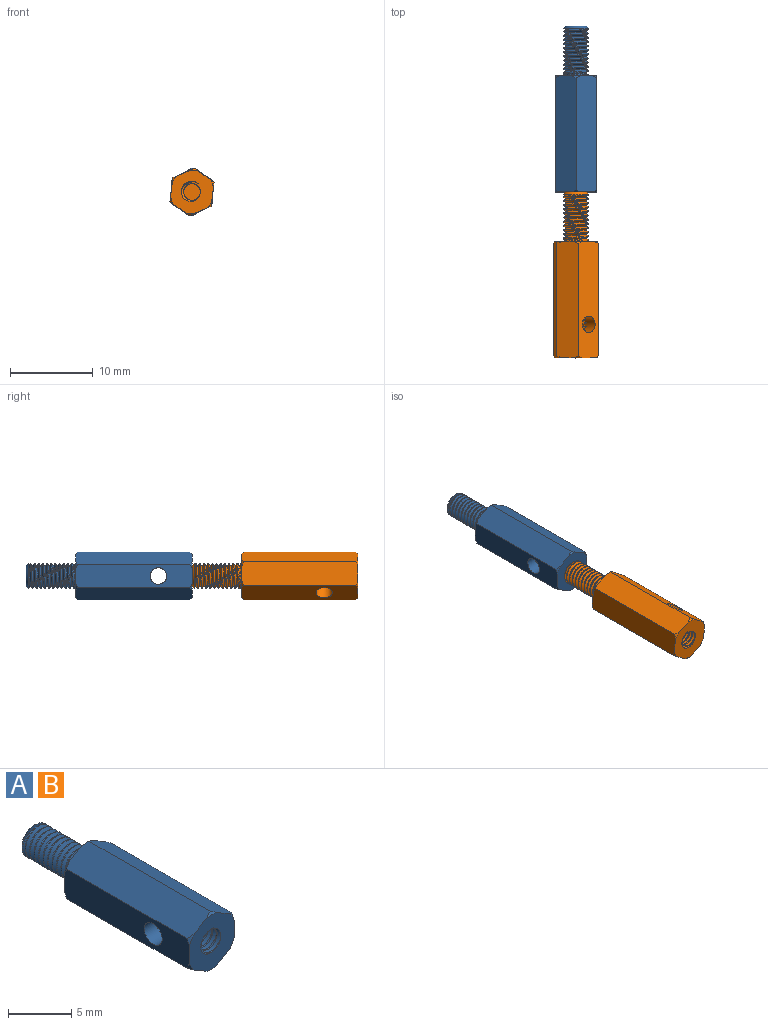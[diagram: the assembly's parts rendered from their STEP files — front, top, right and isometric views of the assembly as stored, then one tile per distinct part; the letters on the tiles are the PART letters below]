
ASSEMBLY  parts=2 mates=1
PART A: 76 faces, bbox 5.6x20.3x5.9 mm
  f0: bspline ~3.57x2.93mm, area 14.5mm2, adj f14,f26,f41,f59,f74,f75
  f1: bspline ~2.57x1.91mm, area 0.6mm2, adj f15,f24,f74,f75
  f2: bspline ~2.2x0.77mm, area 0.4mm2, adj f16,f27,f74,f75
  f3: bspline ~2.2x0.77mm, area 0.3mm2, adj f17,f25,f74,f75
  f4: bspline ~2.2x0.77mm, area 0.4mm2, adj f18,f23,f74,f75
  f5: bspline ~2.2x0.77mm, area 0.4mm2, adj f19,f22,f74,f75
  f6: bspline ~2.2x0.77mm, area 0.6mm2, adj f20,f28,f74,f75
  f7: bspline ~3.57x2.93mm, area 14.6mm2, adj f14,f15,f41,f59,f74,f75
  f8: bspline ~2.2x0.77mm, area 0.6mm2, adj f16,f26,f74,f75
  f9: bspline ~2.2x0.77mm, area 0.4mm2, adj f17,f24,f74,f75
  f10: bspline ~2.2x0.77mm, area 0.3mm2, adj f18,f27,f74,f75
  f11: bspline ~2.2x0.77mm, area 0.3mm2, adj f19,f29,f74,f75
  f12: bspline ~2.2x0.77mm, area 0.4mm2, adj f20,f23,f74,f75
  f13: bspline ~2.57x1.91mm, area 0.6mm2, adj f21,f22,f74,f75
  f14: bspline ~3.4x2.99mm, area 3.7mm2, adj f0,f7,f41,f74
  f15: bspline ~2.61x1.94mm, area 0.2mm2, adj f1,f7,f74,f75
  f16: bspline ~2.24x0.66mm, area 0.2mm2, adj f2,f8,f74,f75
  f17: bspline ~2.24x0.66mm, area 0.1mm2, adj f3,f9,f74,f75
  f18: bspline ~2.24x0.66mm, area 0.1mm2, adj f4,f10,f74,f75
  f19: bspline ~2.24x0.66mm, area 0.1mm2, adj f5,f11,f74,f75
  f20: bspline ~2.24x0.66mm, area 0.2mm2, adj f6,f12,f74,f75
  f21: bspline ~2.61x1.94mm, area 0.2mm2, adj f13,f53,f74,f75
  f22: cylinder r=1mm len=1.16mm, axis (0,-1,0), area 0.1mm2, adj f5,f13,f74,f75
  f23: cylinder r=1mm len=0.65mm, axis (0,-1,0), area 0.1mm2, adj f4,f12,f74,f75
  f24: cylinder r=1mm len=1.11mm, axis (0,-1,0), area 0.1mm2, adj f1,f9,f74,f75
  f25: cylinder r=1mm len=0.1mm, axis (0,-1,0), area 0mm2, adj f3,f74,f75
  f26: cylinder r=1mm len=1.62mm, axis (0,-1,0), area 0.2mm2, adj f0,f8,f74,f75
  f27: cylinder r=1mm len=0.61mm, axis (0,-1,0), area 0.1mm2, adj f2,f10,f74,f75
  f28: cylinder r=1mm len=1.67mm, axis (0,-1,0), area 0.2mm2, adj f6,f54,f74,f75
  f29: cylinder r=1mm len=0.15mm, axis (0,-1,0), area 0mm2, adj f11,f74,f75
  f30: cylinder r=1mm len=0.97mm, axis (0,-1,0), area 0.1mm2, adj f31,f53,f54,f74
  f31: cylinder r=1mm len=2mm, axis (0,-1,0), area 0.8mm2, adj f30,f32,f53,f54
  f32: cylinder r=1mm len=2mm, axis (0,-1,0), area 1.2mm2, adj f31,f33,f53,f55
  f33: cylinder r=1mm len=4mm, axis (0,-1,0), area 24mm2, adj f32,f55,f56,f60,f61
  f34: plane 14.05x2.55mm, normal (0.5,0,0.87), area 40.1mm2, adj f35,f39,f41,f42,f62,f65,f72,f73
  f35: plane 14.05x2.55mm, normal (-0.5,0,0.87), area 40.1mm2, adj f34,f36,f41,f42,f70,f71,f72,f73
  f36: plane 14.05x2.94mm, normal (-1,0,0), area 37mm2, adj f35,f37,f41,f42,f68,f69,f70,f71
  f37: plane 14.05x2.55mm, normal (-0.5,0,-0.87), area 40.1mm2, adj f36,f38,f41,f42,f66,f67,f68,f69
  f38: plane 14.05x2.55mm, normal (0.5,0,-0.87), area 40.1mm2, adj f37,f39,f41,f42,f63,f64,f66,f67
  f39: plane 14.05x2.94mm, normal (1,0,0), area 37mm2, adj f34,f38,f41,f42,f62,f63,f64,f65
  f40: cylinder r=1.5mm len=5.75mm, axis (0,-1,0), area 5mm2, adj f42,f44,f45,f47,f49,f50,f51
  f41: plane 5.41x5.14mm, normal (0,-1,0), area 16.9mm2, adj f0,f7,f14,f34,f35,f36,f37,f38
  f42: plane 5.29x5.01mm, normal (0,1,0), area 14mm2, adj f34,f35,f36,f37,f38,f39,f40,f45
  f43: plane 2.5x2.5mm, normal (0,1,0), area 4.9mm2, adj f44
  f44: cone r=1.5mm half-angle=45deg, axis (0,-1,0), area 3.1mm2, adj f40,f43,f52
  f45: plane 0.04x0.04mm, normal (-1,-0.01,0), area 0mm2, adj f40,f42,f46,f51
  f46: bspline ~2.85x2.73mm, area 1.1mm2, adj f42,f45,f47,f48,f51
  f47: bspline ~3.25x3.12mm, area 1.4mm2, adj f40,f42,f46,f50
  f48: bspline ~5.54x2.84mm, area 11.3mm2, adj f46,f49,f50,f52
  f49: bspline ~5.41x3.46mm, area 27.6mm2, adj f40,f48,f51,f52
  f50: bspline ~5.66x3.46mm, area 29.2mm2, adj f40,f47,f48,f52
  f51: bspline ~3.39x3.28mm, area 1.5mm2, adj f40,f45,f46,f49
  f52: plane 3.14x3.14mm, normal (0,-1,0), area 1.4mm2, adj f44,f48,f49,f50
  f53: bspline ~2.93x2.54mm, area 4.7mm2, adj f21,f30,f31,f32,f56,f58,f74,f75
  f54: bspline ~2.54x2.54mm, area 3.7mm2, adj f28,f30,f31,f55,f58,f74,f75
  f55: bspline ~2.42x2.29mm, area 1.2mm2, adj f32,f33,f54,f57,f60
  f56: bspline ~2.42x2.29mm, area 1.2mm2, adj f33,f53,f57,f60
  f57: bspline ~2.45x2.32mm, area 0.5mm2, adj f55,f56,f58,f60
  f58: bspline ~2.99x2.59mm, area 1mm2, adj f53,f54,f57,f75
  f59: cylinder r=1mm len=3.21mm, axis (0,-1,0), area 4.5mm2, adj f0,f7,f41,f75
  f60: plane 0.09x0.04mm, normal (1,-0.02,-0.01), area 0mm2, adj f33,f55,f56,f57
  f61: plane 2x2mm, normal (0,-1,0), area 3.1mm2, adj f33
  f62: cone r=2.64mm half-angle=45deg, axis (0,-1,0), area 0.2mm2, adj f34,f39,f42
  f63: cone r=2.64mm half-angle=45deg, axis (0,-1,0), area 0.2mm2, adj f38,f39,f42
  f64: cone r=2.89mm half-angle=45deg, axis (0,1,0), area 0.2mm2, adj f38,f39,f41
  f65: cone r=2.89mm half-angle=45deg, axis (0,1,0), area 0.2mm2, adj f34,f39,f41
  f66: cone r=2.64mm half-angle=45deg, axis (0,-1,0), area 0.2mm2, adj f37,f38,f42
  f67: cone r=2.89mm half-angle=45deg, axis (0,1,0), area 0.2mm2, adj f37,f38,f41
  f68: cone r=2.64mm half-angle=45deg, axis (0,-1,0), area 0.2mm2, adj f36,f37,f42
  f69: cone r=2.89mm half-angle=45deg, axis (0,1,0), area 0.2mm2, adj f36,f37,f41
  f70: cone r=2.64mm half-angle=45deg, axis (0,-1,0), area 0.2mm2, adj f35,f36,f42
  f71: cone r=2.89mm half-angle=45deg, axis (0,1,0), area 0.2mm2, adj f35,f36,f41
  f72: cone r=2.64mm half-angle=45deg, axis (0,-1,0), area 0.2mm2, adj f34,f35,f42
  f73: cone r=2.89mm half-angle=45deg, axis (0,1,0), area 0.2mm2, adj f34,f35,f41
  f74: cylinder r=1mm len=2.5mm, axis (-1,0,0), area 10.6mm2, adj f0,f1,f2,f3,f4,f5,f6,f7
  f75: cylinder r=1mm len=2.5mm, axis (-1,0,0), area 10.5mm2, adj f0,f1,f2,f3,f4,f5,f6,f7
PART B: same geometry as A
PLACE A t=(-12.1,8.16,-15.22)mm fixed
PLACE B rot(axis=(0,-1,0),53deg) t=(-12.1,-11.84,-15.22)mm
MATE revolute B.f22 <-> A.f22  axis (0,-1,0) through (-12.1,-24.22,-15.22)mm
